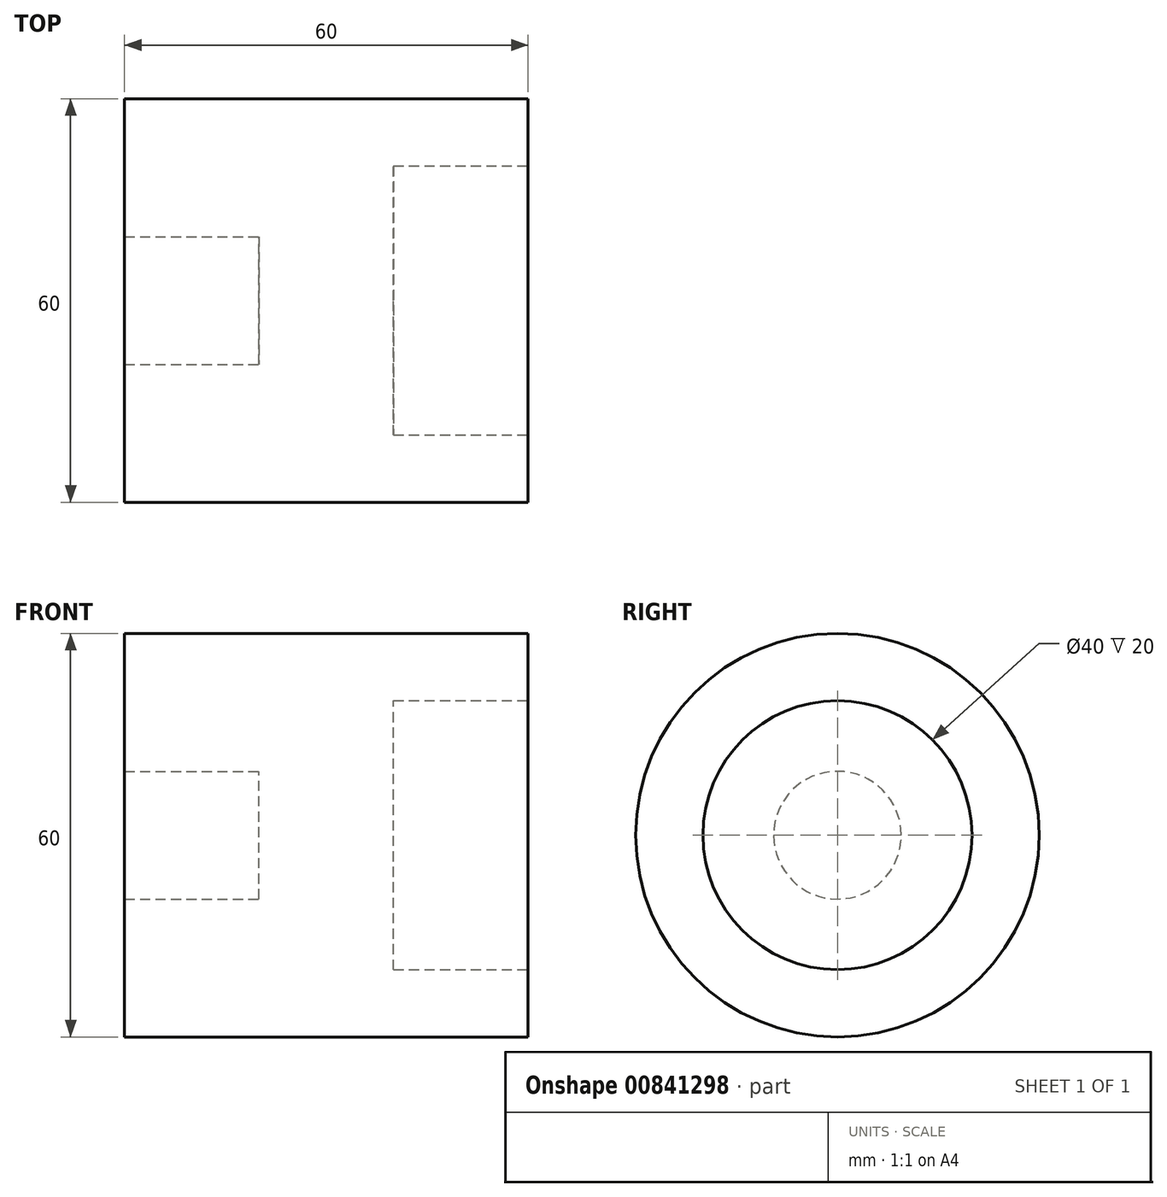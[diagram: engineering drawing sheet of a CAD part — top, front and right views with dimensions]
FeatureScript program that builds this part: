
annotation { "Feature Type Name" : "Feature", "Feature Type Description" : "" }
export const myFeature = defineFeature(function(context is Context, id is Id, definition is map)
    precondition{}
    {
        {
            var Q0;
            Q0=qCreatedBy(makeId("Front.planeOp"),FACE);
            var sketch = newSketch(context, id + "F0", { "sketchPlane" : qUnion([Q0])});
            skLineSegment(sketch, "E0.bottom", {"start": v(-47.87, 30) * mm, "end": v(12.13, 30) * mm});
            skLineSegment(sketch, "E0.left", {"start": v(-47.87, 30) * mm, "end": v(-47.87, 9.5) * mm});
            skPoint(sketch, "E0.middle", {"position": v(0, 0) * mm});
            skLineSegment(sketch, "E1", {"start": v(-47.87, 9.5) * mm, "end": v(-27.87, 9.5) * mm});
            skLineSegment(sketch, "E2", {"start": v(-27.87, 9.5) * mm, "end": v(-27.87, 0) * mm});
            skLineSegment(sketch, "E3", {"start": v(12.13, 30) * mm, "end": v(12.13, 20) * mm});
            skLineSegment(sketch, "E4", {"start": v(12.13, 20) * mm, "end": v(-7.87, 20) * mm});
            skLineSegment(sketch, "E5", {"start": v(-7.87, 20) * mm, "end": v(-7.87, 0) * mm});
            skLineSegment(sketch, "E6", {"start": v(-7.87, 0) * mm, "end": v(-27.87, 0) * mm});
            skSolve(sketch);
        }
        {
            var Q0;
            Q0 = qSketchRegion(id + "F0", true);
            var Q1;
            Q1=sQuery(id+"F0.wireOp",EDGE,"E6");
            revolve(context, id + "F1", {"surfaceOperationType" : NewSurfaceOperationType.NEW, "entities" : qUnion([Q0]), "axis" : qUnion([Q1]), "revolveType" : RevolveType.FULL});
        }
    });
